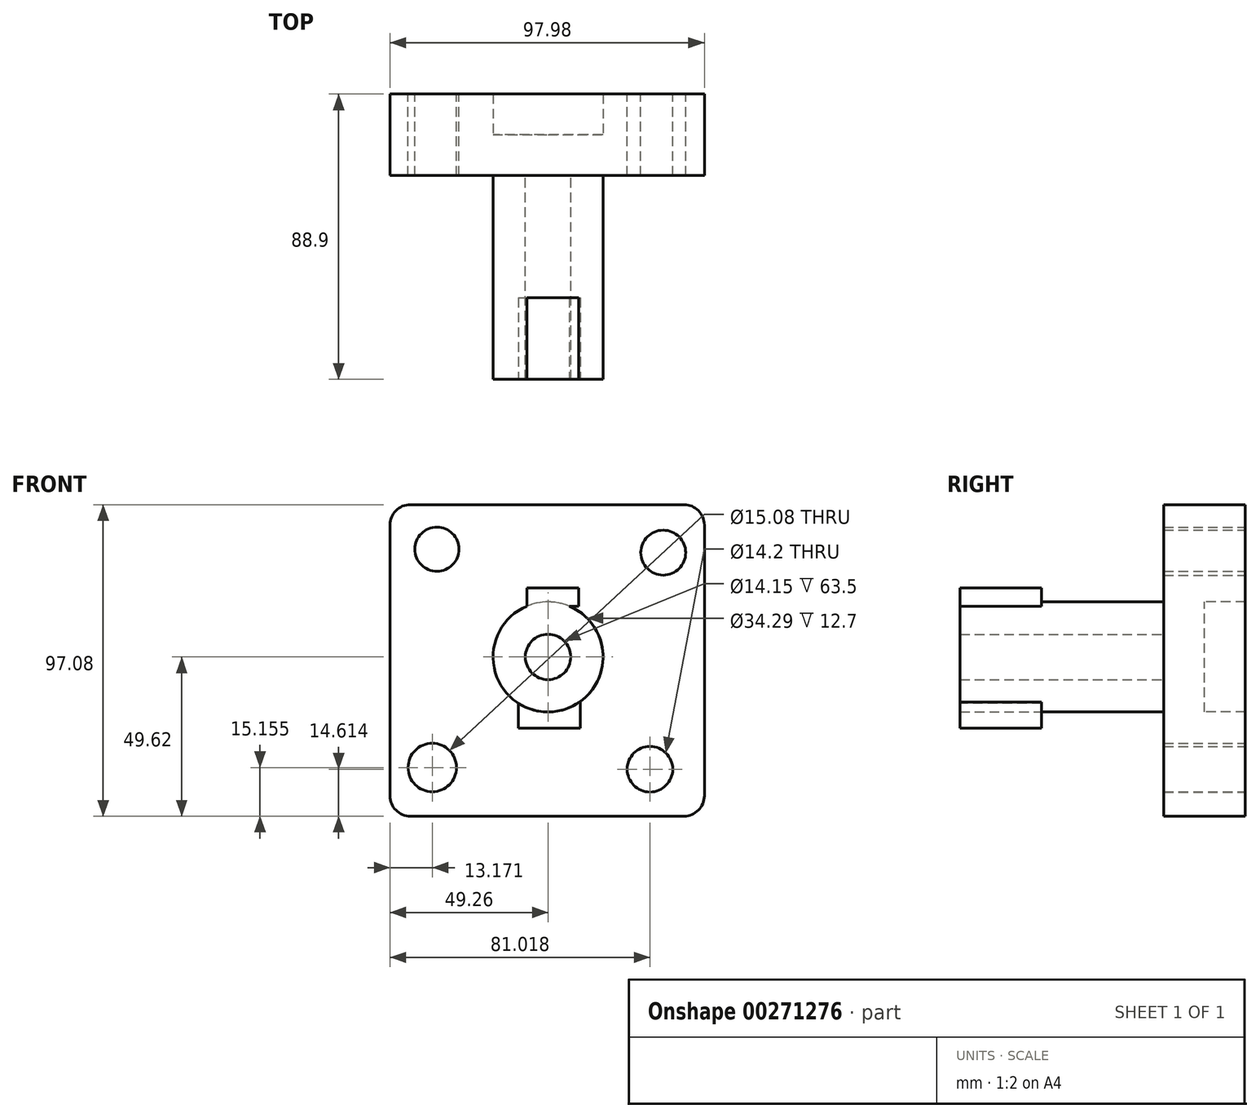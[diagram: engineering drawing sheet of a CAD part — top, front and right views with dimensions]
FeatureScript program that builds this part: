
annotation { "Feature Type Name" : "Feature", "Feature Type Description" : "" }
export const myFeature = defineFeature(function(context is Context, id is Id, definition is map)
    precondition{}
    {
        {
            var Q0;
            Q0=qCreatedBy(makeId("Front.planeOp"),FACE);
            var sketch = newSketch(context, id + "F0", { "sketchPlane" : qUnion([Q0])});
            skLineSegment(sketch, "E0.bottom", {"start": v(-42.91, 47.46) * mm, "end": v(42.37, 47.46) * mm});
            skLineSegment(sketch, "E0.top", {"start": v(-42.91, -49.62) * mm, "end": v(42.37, -49.62) * mm});
            skLineSegment(sketch, "E0.left", {"start": v(-49.26, 41.1) * mm, "end": v(-49.26, -43.27) * mm});
            skLineSegment(sketch, "E0.right", {"start": v(48.72, 41.1) * mm, "end": v(48.72, -43.27) * mm});
            skPoint(sketch, "E1.visualSharp", {"position": v(-49.26, 47.46) * mm});
            skArc(sketch, "E1.filletArc", {"start": v(-42.91, 47.46) * mm, "mid": v(-47.4, 45.6) * mm, "end": v(-49.26, 41.1) * mm});
            skPoint(sketch, "E2.visualSharp", {"position": v(48.72, -49.62) * mm});
            skArc(sketch, "E2.filletArc", {"start": v(42.37, -49.62) * mm, "mid": v(46.86, -47.76) * mm, "end": v(48.72, -43.27) * mm});
            skPoint(sketch, "E3.visualSharp", {"position": v(48.72, 47.46) * mm});
            skArc(sketch, "E3.filletArc", {"start": v(48.72, 41.1) * mm, "mid": v(46.86, 45.6) * mm, "end": v(42.37, 47.46) * mm});
            skPoint(sketch, "E4.visualSharp", {"position": v(-49.26, -49.62) * mm});
            skArc(sketch, "E4.filletArc", {"start": v(-49.26, -43.27) * mm, "mid": v(-47.4, -47.76) * mm, "end": v(-42.91, -49.62) * mm});
            skCircle(sketch, "E5", {"center": v(35.9, 32.48) * mm, "radius": 7 * mm});
            skCircle(sketch, "E6", {"center": v(-34.65, 33.56) * mm, "radius": 6.87 * mm});
            skCircle(sketch, "E7", {"center": v(-36.09, -34.46) * mm, "radius": 7.54 * mm});
            skCircle(sketch, "E8", {"center": v(31.76, -35) * mm, "radius": 7.1 * mm});
            skSolve(sketch);
        }
        {
            var Q0;
            Q0=makeQuery(id+"F0.imprint","IMPRINT",FACE,{"disambiguationData":[TD([[makeQuery(id+"F0.imprint","IMPRINT",EDGE,{"derivedFrom":sQuery(id+"F0.wireOp",EDGE,"E0.bottom")}),-1.0]])]});
            extrude(context, id + "F1", {"entities" : qUnion([Q0]), "depth" : 12.7 * mm});
        }
        {
            var Q0;
            Q0=makeQuery(id+"F1.opExtrude","CAP_FACE",FACE,{"disambiguationData":[OSD([sQuery(id+"F0.wireOp",EDGE,"E0.bottom"),sQuery(id+"F0.wireOp",EDGE,"E0.top"),sQuery(id+"F0.wireOp",EDGE,"E0.left"),sQuery(id+"F0.wireOp",EDGE,"E0.right"),sQuery(id+"F0.wireOp",EDGE,"E1.filletArc"),sQuery(id+"F0.wireOp",EDGE,"E2.filletArc"),sQuery(id+"F0.wireOp",EDGE,"E3.filletArc"),sQuery(id+"F0.wireOp",EDGE,"E4.filletArc"),sQuery(id+"F0.wireOp",EDGE,"E5"),sQuery(id+"F0.wireOp",EDGE,"E6"),sQuery(id+"F0.wireOp",EDGE,"E7"),sQuery(id+"F0.wireOp",EDGE,"E8")])],"isStart":false});
            var sketch = newSketch(context, id + "F2", { "sketchPlane" : qUnion([Q0])});
            skCircle(sketch, "E9", {"center": v(0, 0) * mm, "radius": 17.15 * mm});
            skCircle(sketch, "E10", {"center": v(0, 0) * mm, "radius": 7.07 * mm});
            skSolve(sketch);
        }
        {
            var Q0;
            Q0=makeQuery(id+"F2.imprint","IMPRINT",FACE,{"disambiguationData":[TD([[makeQuery(id+"F2.imprint","IMPRINT",EDGE,{"derivedFrom":sQuery(id+"F2.wireOp",EDGE,"E9")}),1.0]])]});
            extrude(context, id + "F3", {"entities" : qUnion([Q0]), "operationType" : NewBodyOperationType.ADD, "depth" : 63.5 * mm});
        }
        {
            var Q0;
            Q0=makeQuery(id+"F1.opExtrude","SWEPT_FACE",FACE,{"disambiguationData":[OSD([sQuery(id+"F0.wireOp",EDGE,"E0.top")])]});
            cPlane(context, id + "F4", {"entities" : qUnion([Q0]), "cplaneType" : CPlaneType.OFFSET, "offset" : 31.75 * mm, "oppositeDirection" : true, "width" : 152.4 * mm, "height" : 152.4 * mm});
        }
        {
            var Q0;
            Q0=qCreatedBy(id+"F4.planeOp",FACE);
            var sketch = newSketch(context, id + "F5", { "sketchPlane" : qUnion([Q0])});
            skLineSegment(sketch, "E11.bottom", {"start": v(-7.04, 76.5) * mm, "end": v(9.92, 76.5) * mm});
            skLineSegment(sketch, "E11.top", {"start": v(-7.04, 42.77) * mm, "end": v(9.92, 42.77) * mm});
            skLineSegment(sketch, "E11.left", {"start": v(-7.04, 76.5) * mm, "end": v(-7.04, 42.77) * mm});
            skLineSegment(sketch, "E11.right", {"start": v(9.92, 76.5) * mm, "end": v(9.92, 42.77) * mm});
            skCircle(sketch, "E12", {"center": v(1.44, 68.05) * mm, "radius": 4.73 * mm});
            skPoint(sketch, "E12.centerSnap0", {"position": v(1.44, 76.5) * mm});
            skCircle(sketch, "E13", {"center": v(1.44, 50.53) * mm, "radius": 4.6 * mm});
            skSolve(sketch);
        }
        {
            var Q0;
            Q0 = qSketchRegion(id + "F5", true);
            extrude(context, id + "F6", {"entities" : qUnion([Q0]), "depth" : 5.08 * mm});
        }
        {
            var Q0;
            Q0=makeQuery(id+"F3.opExtrude","CAP_FACE",FACE,{"disambiguationData":[OSD([sQuery(id+"F2.wireOp",EDGE,"E9"),sQuery(id+"F2.wireOp",EDGE,"E10")])],"isStart":false});
            var sketch = newSketch(context, id + "F7", { "sketchPlane" : qUnion([Q0])});
            skLineSegment(sketch, "E14.bottom", {"start": v(-6.64, 15.81) * mm, "end": v(9.57, 15.81) * mm});
            skLineSegment(sketch, "E14.top", {"start": v(-6.64, 21.49) * mm, "end": v(9.57, 21.49) * mm});
            skLineSegment(sketch, "E14.left", {"start": v(-6.64, 15.81) * mm, "end": v(-6.64, 21.49) * mm});
            skLineSegment(sketch, "E14.right", {"start": v(9.57, 15.81) * mm, "end": v(9.57, 21.49) * mm});
            skSolve(sketch);
        }
        {
            var Q0;
            {var subQ0=sQuery(id+"F0.wireOp",EDGE,"E6");var subQ1=sQuery(id+"F0.wireOp",EDGE,"E4.filletArc");var subQ2=sQuery(id+"F0.wireOp",EDGE,"E3.filletArc");var subQ3=sQuery(id+"F0.wireOp",EDGE,"E2.filletArc");var subQ4=sQuery(id+"F0.wireOp",EDGE,"E1.filletArc");var subQ5=sQuery(id+"F0.wireOp",EDGE,"E0.bottom");var subQ6=sQuery(id+"F0.wireOp",EDGE,"E5");var subQ7=sQuery(id+"F0.wireOp",EDGE,"E0.top");var subQ8=sQuery(id+"F0.wireOp",EDGE,"E0.left");var subQ9=sQuery(id+"F0.wireOp",EDGE,"E0.right");var subQ10=sQuery(id+"F0.wireOp",EDGE,"E7");var subQ11=sQuery(id+"F0.wireOp",EDGE,"E8");Q0=makeQuery(id+"F3.boolean.opBoolean","SPLIT",FACE,{"disambiguationData":[TD([makeQuery(id+"F1.opExtrude","SWEPT_FACE",FACE,{"disambiguationData":[OSD([subQ5])]})])],"derivedFrom":makeQuery(id+"F1.opExtrude","CAP_FACE",FACE,{"disambiguationData":[OSD([subQ5,subQ7,subQ8,subQ9,subQ4,subQ3,subQ2,subQ1,subQ6,subQ0,subQ10,subQ11])],"isStart":false})});}
            var Q1;
            Q1=makeQuery(id+"F7.imprint","IMPRINT",FACE,{"disambiguationData":[TD([[makeQuery(id+"F7.imprint","IMPRINT",EDGE,{"derivedFrom":sQuery(id+"F7.wireOp",EDGE,"E14.top")}),-1.0]])]});
            extrude(context, id + "F8", {"entities" : qUnion([Q0, Q1]), "operationType" : NewBodyOperationType.ADD, "oppositeDirection" : true, "depth" : 25.4 * mm});
        }
        {
            var Q0;
            Q0=makeQuery(id+"F6.opExtrude","SWEPT_BODY",BODY,{"disambiguationData":[OSD([sQuery(id+"F5.wireOp",EDGE,"E11.bottom"),sQuery(id+"F5.wireOp",EDGE,"E11.top"),sQuery(id+"F5.wireOp",EDGE,"E11.left"),sQuery(id+"F5.wireOp",EDGE,"E11.right"),sQuery(id+"F5.wireOp",EDGE,"E12"),sQuery(id+"F5.wireOp",EDGE,"E13")])]});
            deleteBodies(context, id + "F9", {"entities" : qUnion([Q0])});
        }
        {
            var Q0;
            Q0=makeQuery(id+"F7.imprint","IMPRINT",FACE,{"disambiguationData":[TD([[makeQuery(id+"F7.imprint","IMPRINT",EDGE,{"derivedFrom":makeQuery(id+"F3.opExtrude","CAP_EDGE",EDGE,{"disambiguationData":[OSD([sQuery(id+"F2.wireOp",EDGE,"E10")])],"isStart":false})}),-1.0]])]});
            var sketch = newSketch(context, id + "F10", { "sketchPlane" : qUnion([Q0])});
            skLineSegment(sketch, "E15.bottom", {"start": v(-9.2, -14.07) * mm, "end": v(10.1, -14.07) * mm});
            skLineSegment(sketch, "E15.top", {"start": v(-9.2, -22.2) * mm, "end": v(10.1, -22.2) * mm});
            skLineSegment(sketch, "E15.left", {"start": v(-9.2, -14.07) * mm, "end": v(-9.2, -22.2) * mm});
            skLineSegment(sketch, "E15.right", {"start": v(10.1, -14.07) * mm, "end": v(10.1, -22.2) * mm});
            skSolve(sketch);
        }
        {
            var Q0;
            {var subQ2=sQuery(id+"F10.wireOp",EDGE,"E15.top");Q0=makeQuery(id+"F10.imprint","IMPRINT",FACE,{"disambiguationData":[TD([[makeQuery(id+"F10.imprint","IMPRINT",EDGE,{"derivedFrom":subQ2}),1.0]])]});}
            extrude(context, id + "F11", {"entities" : qUnion([Q0]), "oppositeDirection" : true, "depth" : 25.4 * mm});
        }
    });
